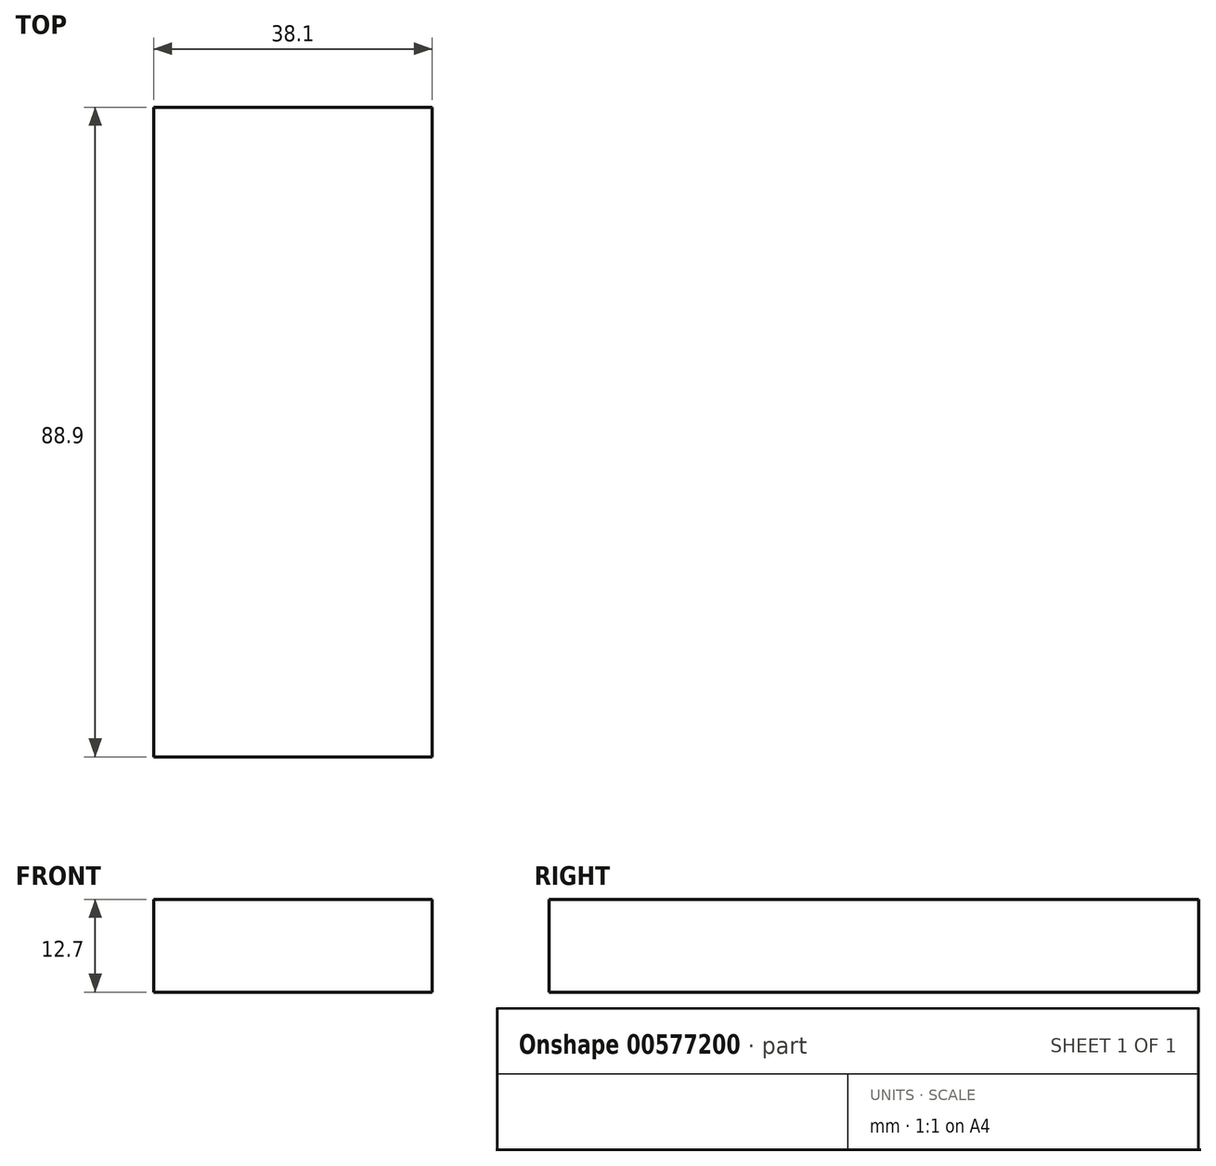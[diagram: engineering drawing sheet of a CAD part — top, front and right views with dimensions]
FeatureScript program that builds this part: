
annotation { "Feature Type Name" : "Feature", "Feature Type Description" : "" }
export const myFeature = defineFeature(function(context is Context, id is Id, definition is map)
    precondition{}
    {
        {
            var Q0;
            Q0=qCreatedBy(makeId("Top.planeOp"),FACE);
            var sketch = newSketch(context, id + "F0", { "sketchPlane" : qUnion([Q0])});
            skLineSegment(sketch, "E0.bottom", {"start": v(-48.58, 54.17) * mm, "end": v(-10.48, 54.17) * mm});
            skLineSegment(sketch, "E0.top", {"start": v(-48.58, -34.73) * mm, "end": v(-10.48, -34.73) * mm});
            skLineSegment(sketch, "E0.left", {"start": v(-48.58, 54.17) * mm, "end": v(-48.58, -34.73) * mm});
            skLineSegment(sketch, "E0.right", {"start": v(-10.48, 54.17) * mm, "end": v(-10.48, -34.73) * mm});
            skSolve(sketch);
        }
        {
            var Q0;
            Q0=makeQuery(id+"F0.imprint","IMPRINT",FACE,{"disambiguationData":[TD([[makeQuery(id+"F0.imprint","IMPRINT",EDGE,{"derivedFrom":sQuery(id+"F0.wireOp",EDGE,"E0.bottom")}),-1.0]])]});
            extrude(context, id + "F1", {"entities" : qUnion([Q0]), "depth" : 12.7 * mm, "offsetDistance" : 25.4 * mm});
        }
    });
